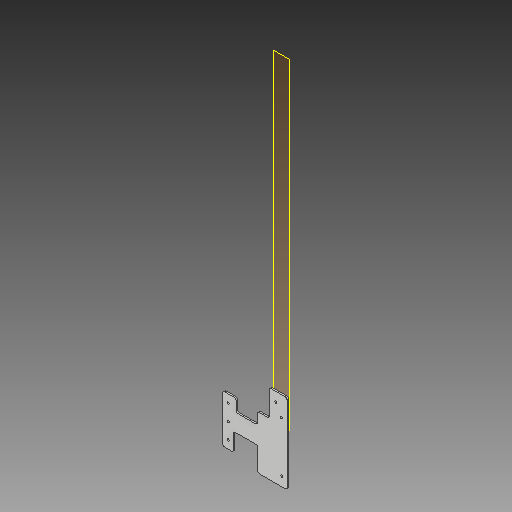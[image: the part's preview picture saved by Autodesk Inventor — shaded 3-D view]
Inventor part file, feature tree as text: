
AUTODESK INVENTOR PART (.ipt)
format: ipt  version: 2018 (Build 220112000, 112)  size: 168,448 bytes
history: native  units: mm
features: extrude x2, sketch x2, plane x1, fillet x1
ambient origin geometry x8: Origin, YZ Plane, XZ Plane, XY Plane, X Axis, Y Axis, Z Axis, Center Point
bodies: Solid1 (feature_tree)
feature tree (6):
  plane  "Work Plane1"
  extrude  "Extrusion1"  Depth=6.0mm TaperAngle=0.0deg
  fillet  "Fillet1"  Radius=92.0mm
  extrude  "Extrusion2"  Depth=40.0mm
  sketch  "Sketch1"  dims[d0=110.0mm d2=6.0mm d3=0.0mm d4=92.0mm]
  sketch  "Sketch2"  dims[d5=68.0mm d6=40.0mm d7=180.0mm d8=50.0mm d9=46.0mm d10=300.0mm d11=7.0mm d12=80.0mm d13=44.0mm d14=45.0mm d15=100.0mm d17=8.0mm d18=60.0mm d19=60.0mm d20=8.0mm d21=35.0mm d22=20.0mm d23=35.0mm d24=25.0mm d25=40.0mm d26=20.0mm d27=30.0mm d28=10.0mm d29=0.0mm]
